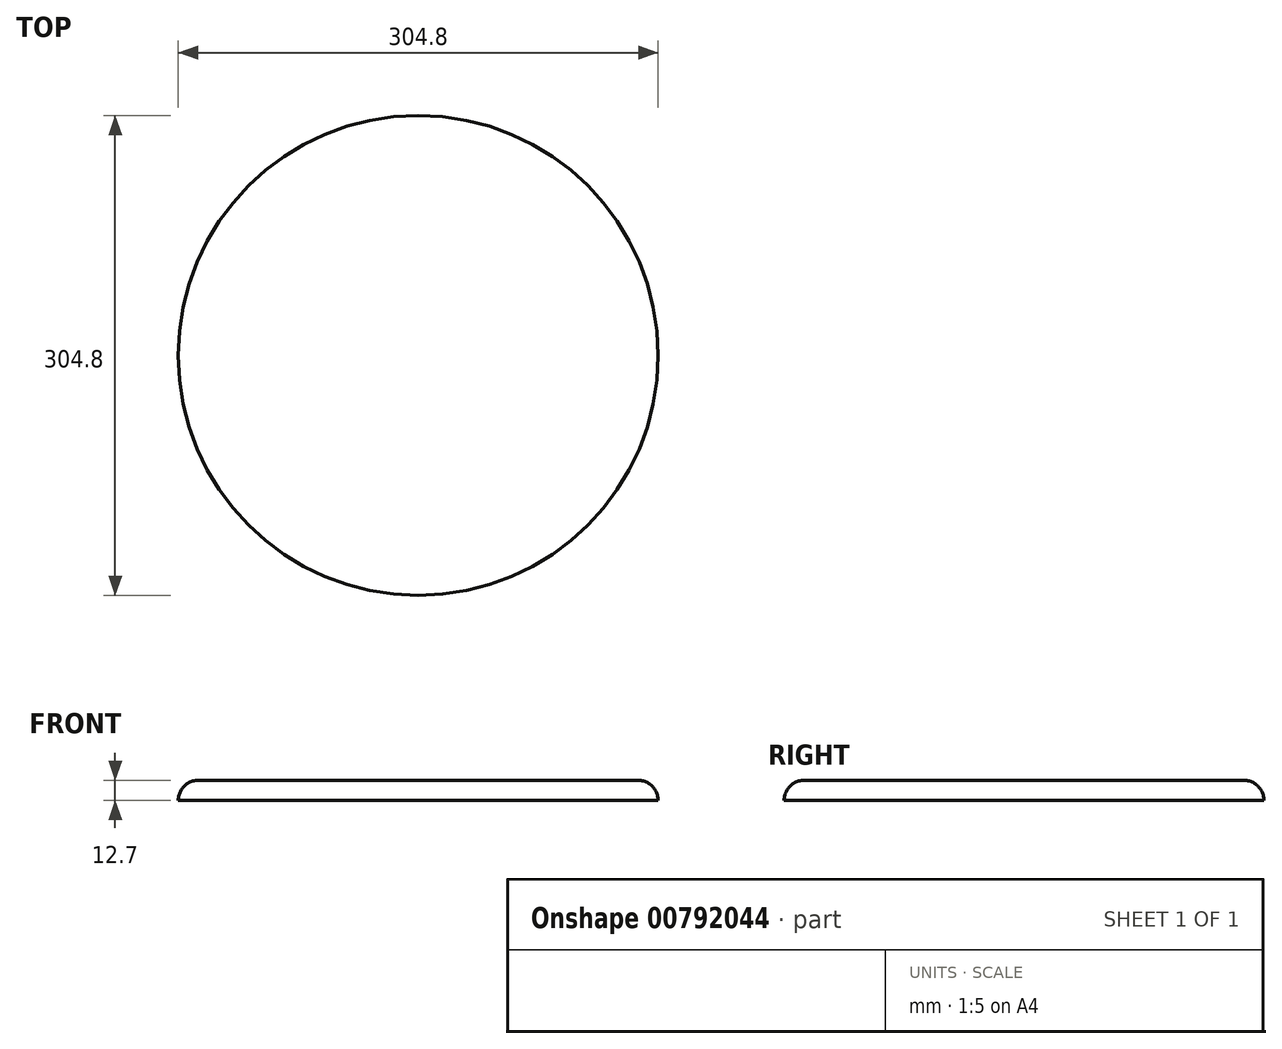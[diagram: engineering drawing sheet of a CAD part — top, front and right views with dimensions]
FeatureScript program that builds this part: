
annotation { "Feature Type Name" : "Feature", "Feature Type Description" : "" }
export const myFeature = defineFeature(function(context is Context, id is Id, definition is map)
    precondition{}
    {
        {
            var Q0;
            Q0=qCreatedBy(makeId("Front.planeOp"),FACE);
            var sketch = newSketch(context, id + "F0", { "sketchPlane" : qUnion([Q0])});
            skLineSegment(sketch, "E0", {"start": v(0, 0) * mm, "end": v(139.7, 0) * mm});
            skLineSegment(sketch, "E1", {"start": v(152.4, -12.7) * mm, "end": v(152.4, -12.7) * mm});
            skLineSegment(sketch, "E2", {"start": v(152.4, -12.7) * mm, "end": v(0, -12.7) * mm});
            skLineSegment(sketch, "E3", {"start": v(0, -12.7) * mm, "end": v(0, 0) * mm});
            skPoint(sketch, "E4.visualSharp", {"position": v(152.4, 0) * mm});
            skArc(sketch, "E4.filletArc", {"start": v(152.4, -12.7) * mm, "mid": v(148.68, -3.72) * mm, "end": v(139.7, 0) * mm});
            skSolve(sketch);
        }
        {
            var Q0;
            Q0=makeQuery(id+"F0.imprint","IMPRINT",FACE,{"disambiguationData":[TD([[makeQuery(id+"F0.imprint","IMPRINT",EDGE,{"derivedFrom":sQuery(id+"F0.wireOp",EDGE,"E0")}),-1.0]])]});
            var Q1;
            Q1=sQuery(id+"F0.wireOp",EDGE,"E3");
            revolve(context, id + "F1", {"surfaceOperationType" : NewSurfaceOperationType.NEW, "entities" : qUnion([Q0]), "axis" : qUnion([Q1]), "revolveType" : RevolveType.FULL});
        }
    });
